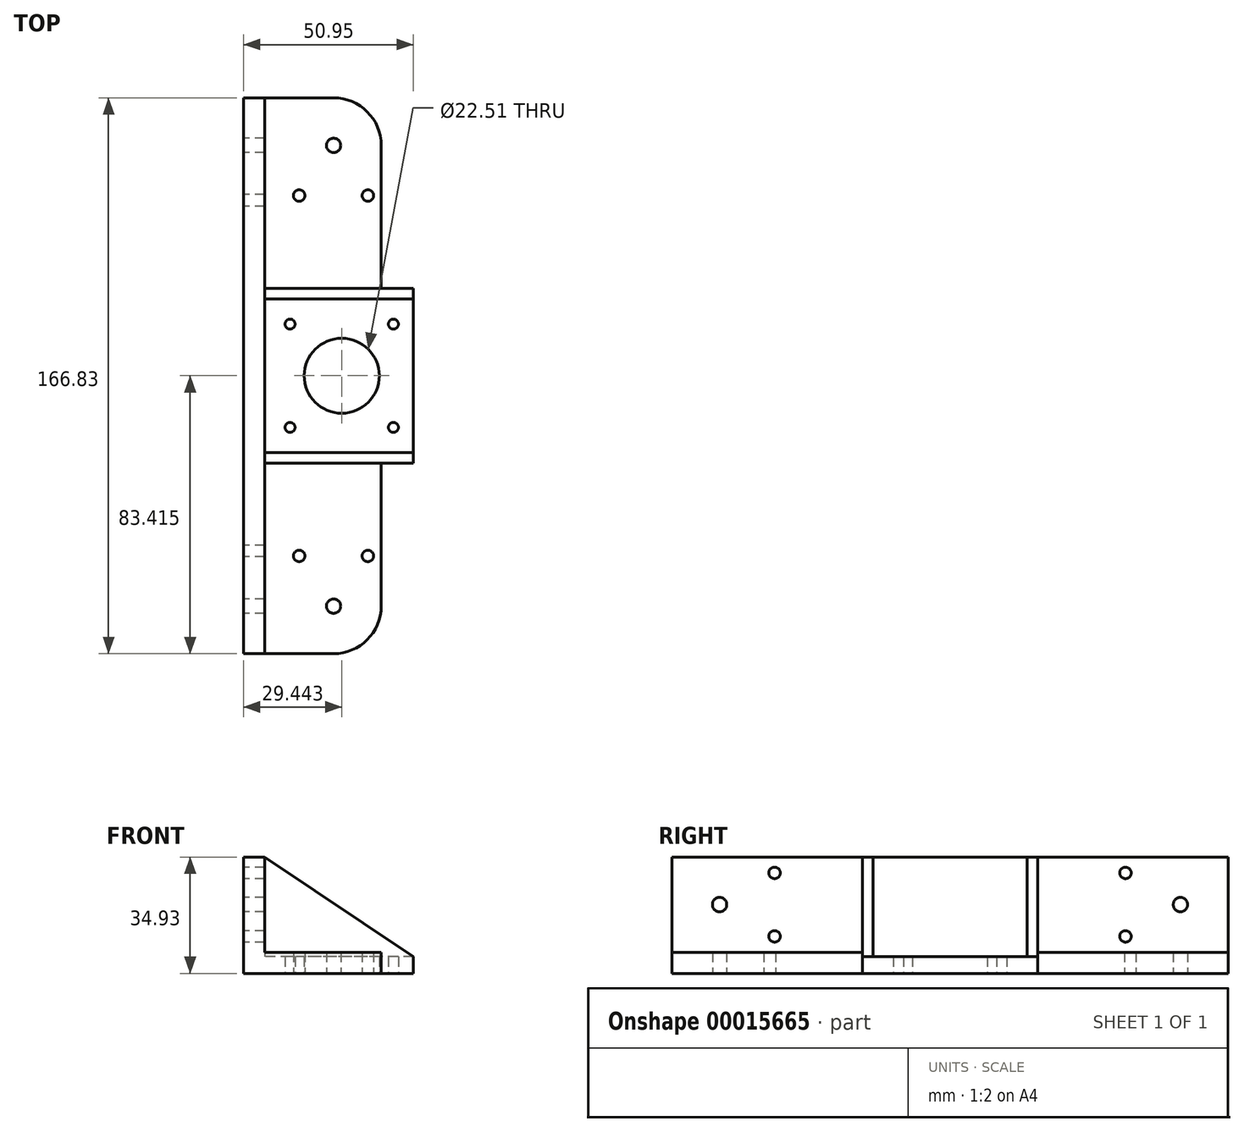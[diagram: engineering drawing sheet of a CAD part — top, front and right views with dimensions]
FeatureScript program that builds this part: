
annotation { "Feature Type Name" : "Feature", "Feature Type Description" : "" }
export const myFeature = defineFeature(function(context is Context, id is Id, definition is map)
    precondition{}
    {
        {
            var Q0;
            Q0=qCreatedBy(makeId("Top.planeOp"),FACE);
            var sketch = newSketch(context, id + "F0", { "sketchPlane" : qUnion([Q0])});
            skLineSegment(sketch, "E0.bottom", {"start": v(0, 0) * mm, "end": v(-26.99, 0) * mm});
            skLineSegment(sketch, "E0.top", {"start": v(0, 166.83) * mm, "end": v(-26.99, 166.83) * mm});
            skLineSegment(sketch, "E0.right", {"start": v(-26.99, 0) * mm, "end": v(-26.99, 166.83) * mm});
            skLineSegment(sketch, "E1.bottom", {"start": v(14.29, 57.15) * mm, "end": v(23.96, 57.15) * mm});
            skLineSegment(sketch, "E1.top", {"start": v(14.29, 109.68) * mm, "end": v(23.96, 109.68) * mm});
            skLineSegment(sketch, "E1.right", {"start": v(23.96, 57.15) * mm, "end": v(23.96, 109.68) * mm});
            skCircle(sketch, "E2", {"center": v(2.45, 83.42) * mm, "radius": 11.25 * mm});
            skLineSegment(sketch, "E3.bottom", {"start": v(17.95, 98.92) * mm, "end": v(-13.05, 98.92) * mm, "construction": true});
            skLineSegment(sketch, "E3.top", {"start": v(17.95, 67.92) * mm, "end": v(-13.05, 67.92) * mm, "construction": true});
            skLineSegment(sketch, "E3.left", {"start": v(17.95, 98.92) * mm, "end": v(17.95, 67.92) * mm, "construction": true});
            skLineSegment(sketch, "E3.right", {"start": v(-13.05, 98.92) * mm, "end": v(-13.05, 67.92) * mm, "construction": true});
            skCircle(sketch, "E4", {"center": v(-13.05, 67.92) * mm, "radius": 1.5 * mm});
            skCircle(sketch, "E5", {"center": v(17.95, 67.92) * mm, "radius": 1.5 * mm});
            skCircle(sketch, "E6", {"center": v(17.95, 98.92) * mm, "radius": 1.5 * mm});
            skCircle(sketch, "E7", {"center": v(-13.05, 98.92) * mm, "radius": 1.5 * mm});
            skLineSegment(sketch, "E8", {"start": v(23.96, 83.42) * mm, "end": v(2.45, 83.42) * mm, "construction": true});
            skLineSegment(sketch, "E9", {"start": v(2.45, 83.42) * mm, "end": v(-26.99, 83.42) * mm, "construction": true});
            skArc(sketch, "E10", {"start": v(0, 0) * mm, "mid": v(10.1, 4.18) * mm, "end": v(14.29, 14.29) * mm});
            skCircle(sketch, "E11", {"center": v(0, 14.29) * mm, "radius": 2.15 * mm});
            skLineSegment(sketch, "E12", {"start": v(14.29, 14.29) * mm, "end": v(14.29, 57.15) * mm});
            skLineSegment(sketch, "E13", {"start": v(14.29, 109.68) * mm, "end": v(14.29, 152.54) * mm});
            skArc(sketch, "E14", {"start": v(14.29, 152.54) * mm, "mid": v(10.1, 162.65) * mm, "end": v(0, 166.83) * mm});
            skCircle(sketch, "E15", {"center": v(0, 152.54) * mm, "radius": 2.15 * mm});
            skLineSegment(sketch, "E16", {"start": v(0, 14.29) * mm, "end": v(0, 29.35) * mm, "construction": true});
            skLineSegment(sketch, "E17", {"start": v(0, 152.54) * mm, "end": v(0, 137.48) * mm, "construction": true});
            skLineSegment(sketch, "E18", {"start": v(-10.32, 137.48) * mm, "end": v(10.32, 137.48) * mm, "construction": true});
            skLineSegment(sketch, "E19", {"start": v(-10.32, 29.35) * mm, "end": v(10.32, 29.35) * mm, "construction": true});
            skCircle(sketch, "E20", {"center": v(-10.32, 29.35) * mm, "radius": 1.73 * mm});
            skCircle(sketch, "E21", {"center": v(10.32, 29.35) * mm, "radius": 1.73 * mm});
            skCircle(sketch, "E22", {"center": v(10.32, 137.48) * mm, "radius": 1.73 * mm});
            skCircle(sketch, "E23", {"center": v(-10.32, 137.48) * mm, "radius": 1.73 * mm});
            skSolve(sketch);
        }
        {
            var Q0;
            Q0 = qSketchRegion(id + "F0", true);
            extrude(context, id + "F1", {"entities" : qUnion([Q0]), "depth" : 5 * mm});
        }
        {
            var Q0;
            Q0=makeQuery(id+"F1.opExtrude","CAP_FACE",FACE,{"disambiguationData":[OSD([sQuery(id+"F0.wireOp",EDGE,"E0.bottom"),sQuery(id+"F0.wireOp",EDGE,"E0.top"),sQuery(id+"F0.wireOp",EDGE,"E0.right"),sQuery(id+"F0.wireOp",EDGE,"sP7DqY9h-m76k-f1Jz-QuWS-NhhGwzX337UM"),sQuery(id+"F0.wireOp",EDGE,"sKsMqQWI-qyKk-qNbw-9HCz-SAMZVSBw6t0P"),sQuery(id+"F0.wireOp",EDGE,"E1.bottom"),sQuery(id+"F0.wireOp",EDGE,"E1.top"),sQuery(id+"F0.wireOp",EDGE,"E1.right")])],"isStart":false});
            var sketch = newSketch(context, id + "F2", { "sketchPlane" : qUnion([Q0])});
            skLineSegment(sketch, "E24.left", {"start": v(-26.99, 0) * mm, "end": v(-26.99, 166.83) * mm});
            skLineSegment(sketch, "E25.top", {"start": v(-20.64, 57.15) * mm, "end": v(23.96, 57.15) * mm});
            skLineSegment(sketch, "E25.left", {"start": v(-20.64, 0) * mm, "end": v(-20.64, 57.15) * mm});
            skLineSegment(sketch, "E26.bottom", {"start": v(23.96, 109.68) * mm, "end": v(-20.64, 109.68) * mm});
            skLineSegment(sketch, "E27", {"start": v(23.96, 57.15) * mm, "end": v(23.96, 60.33) * mm});
            skLineSegment(sketch, "E28", {"start": v(23.96, 109.68) * mm, "end": v(23.96, 106.5) * mm});
            skLineSegment(sketch, "E29.bottom", {"start": v(23.96, 60.33) * mm, "end": v(-20.64, 60.33) * mm});
            skLineSegment(sketch, "E29.top", {"start": v(23.96, 106.5) * mm, "end": v(-20.64, 106.5) * mm});
            skLineSegment(sketch, "E29.left", {"start": v(23.96, 60.33) * mm, "end": v(23.96, 106.5) * mm, "construction": true});
            skLineSegment(sketch, "E29.right", {"start": v(-20.64, 60.33) * mm, "end": v(-20.64, 106.5) * mm});
            skLineSegment(sketch, "E30", {"start": v(-20.64, 109.68) * mm, "end": v(-20.64, 166.83) * mm});
            skLineSegment(sketch, "E31", {"start": v(-20.64, 0) * mm, "end": v(-26.99, 0) * mm});
            skLineSegment(sketch, "E32", {"start": v(-20.64, 166.83) * mm, "end": v(-26.99, 166.83) * mm});
            skSolve(sketch);
        }
        {
            var Q0;
            Q0 = qSketchRegion(id + "F2", true);
            extrude(context, id + "F3", {"entities" : qUnion([Q0]), "operationType" : NewBodyOperationType.ADD, "depth" : 29.93 * mm});
        }
        {
            var Q0;
            Q0=makeQuery(id+"F3.boolean.opBoolean","MERGE",FACE,{"derivedFrom":[makeQuery(id+"F1.opExtrude","SWEPT_FACE",FACE,{"disambiguationData":[OSD([sQuery(id+"F0.wireOp",EDGE,"E1.bottom")])]}),makeQuery(id+"F3.opExtrude","SWEPT_FACE",FACE,{"disambiguationData":[OSD([sQuery(id+"F2.wireOp",EDGE,"E25.top")])]})]});
            var sketch = newSketch(context, id + "F4", { "sketchPlane" : qUnion([Q0])});
            skLineSegment(sketch, "E33.bottom", {"start": v(-20.64, 34.93) * mm, "end": v(23.96, 34.93) * mm});
            skLineSegment(sketch, "E33.top", {"start": v(-20.64, 5) * mm, "end": v(23.96, 5) * mm, "construction": true});
            skLineSegment(sketch, "E33.left", {"start": v(-20.64, 34.93) * mm, "end": v(-20.64, 5) * mm, "construction": true});
            skLineSegment(sketch, "E33.right", {"start": v(23.96, 34.93) * mm, "end": v(23.96, 5) * mm});
            skLineSegment(sketch, "E34", {"start": v(-20.64, 34.93) * mm, "end": v(23.96, 5) * mm});
            skSolve(sketch);
        }
        {
            var Q0;
            Q0 = qSketchRegion(id + "F4", true);
            var Q1;
            Q1=makeQuery(id+"F3.boolean.opBoolean","MERGE",FACE,{"derivedFrom":[makeQuery(id+"F1.opExtrude","SWEPT_FACE",FACE,{"disambiguationData":[OSD([sQuery(id+"F0.wireOp",EDGE,"E1.top")])]}),makeQuery(id+"F3.opExtrude","SWEPT_FACE",FACE,{"disambiguationData":[OSD([sQuery(id+"F2.wireOp",EDGE,"E26.bottom")])]})]});
            extrude(context, id + "F5", {"entities" : qUnion([Q0]), "operationType" : NewBodyOperationType.REMOVE, "endBound" : BoundingType.UP_TO_SURFACE, "oppositeDirection" : true, "endBoundEntityFace" : qUnion([Q1]), "depth" : 25.4 * mm});
        }
        {
            var Q0;
            Q0=makeQuery(id+"F3.boolean.opBoolean","MERGE",FACE,{"derivedFrom":[makeQuery(id+"F1.opExtrude","SWEPT_FACE",FACE,{"disambiguationData":[OSD([sQuery(id+"F0.wireOp",EDGE,"E0.right")])]}),makeQuery(id+"F3.opExtrude","SWEPT_FACE",FACE,{"disambiguationData":[OSD([sQuery(id+"F2.wireOp",EDGE,"E24.left")])]})]});
            var sketch = newSketch(context, id + "F6", { "sketchPlane" : qUnion([Q0])});
            skLineSegment(sketch, "E35", {"start": v(-166.83, 20.64) * mm, "end": v(-152.54, 20.64) * mm, "construction": true});
            skLineSegment(sketch, "E36", {"start": v(0, 20.64) * mm, "end": v(-14.29, 20.64) * mm, "construction": true});
            skCircle(sketch, "E37", {"center": v(-152.54, 20.64) * mm, "radius": 2.15 * mm});
            skCircle(sketch, "E38", {"center": v(-14.29, 20.64) * mm, "radius": 2.15 * mm});
            skLineSegment(sketch, "E39", {"start": v(-83.42, 20.64) * mm, "end": v(-83.42, 34.93) * mm, "construction": true});
            skLineSegment(sketch, "E40.bottom", {"start": v(-136.05, 30.16) * mm, "end": v(-30.79, 30.16) * mm, "construction": true});
            skLineSegment(sketch, "E40.top", {"start": v(-136.05, 11.11) * mm, "end": v(-30.79, 11.11) * mm, "construction": true});
            skLineSegment(sketch, "E40.left", {"start": v(-136.05, 30.16) * mm, "end": v(-136.05, 11.11) * mm, "construction": true});
            skLineSegment(sketch, "E40.right", {"start": v(-30.79, 30.16) * mm, "end": v(-30.79, 11.11) * mm, "construction": true});
            skPoint(sketch, "E40.middle", {"position": v(-83.42, 20.64) * mm});
            skLineSegment(sketch, "E41", {"start": v(-152.54, 20.64) * mm, "end": v(-136.05, 20.64) * mm, "construction": true});
            skCircle(sketch, "E42", {"center": v(-136.05, 30.16) * mm, "radius": 1.73 * mm});
            skCircle(sketch, "E43", {"center": v(-136.05, 11.11) * mm, "radius": 1.73 * mm});
            skCircle(sketch, "E44", {"center": v(-30.79, 11.11) * mm, "radius": 1.73 * mm});
            skCircle(sketch, "E45", {"center": v(-30.79, 30.16) * mm, "radius": 1.73 * mm});
            skLineSegment(sketch, "E46", {"start": v(-83.42, 11.11) * mm, "end": v(-83.42, 5) * mm, "construction": true});
            skSolve(sketch);
        }
        {
            var Q0;
            Q0 = qSketchRegion(id + "F6", true);
            var Q1;
            Q1=makeQuery(id+"F3.opExtrude","SWEPT_FACE",FACE,{"disambiguationData":[OSD([sQuery(id+"F2.wireOp",EDGE,"E29.right")])]});
            extrude(context, id + "F7", {"entities" : qUnion([Q0]), "operationType" : NewBodyOperationType.REMOVE, "endBound" : BoundingType.UP_TO_SURFACE, "oppositeDirection" : true, "endBoundEntityFace" : qUnion([Q1]), "depth" : 25.4 * mm});
        }
        {
            var Q0;
            {var subQ0=sQuery(id+"F0.wireOp",EDGE,"E10");var subQ1=sQuery(id+"F0.wireOp",EDGE,"E1.bottom");var subQ2=sQuery(id+"F0.wireOp",EDGE,"E11");var subQ3=sQuery(id+"F0.wireOp",EDGE,"E0.bottom");var subQ4=sQuery(id+"F0.wireOp",EDGE,"E12");Q0=makeQuery(id+"F3.boolean.opBoolean","SPLIT",FACE,{"disambiguationData":[TD([makeQuery(id+"F1.opExtrude","SWEPT_FACE",FACE,{"disambiguationData":[OSD([subQ3])]})])],"derivedFrom":makeQuery(id+"F1.opExtrude","CAP_FACE",FACE,{"disambiguationData":[OSD([subQ3,sQuery(id+"F0.wireOp",EDGE,"E0.top"),sQuery(id+"F0.wireOp",EDGE,"E0.right"),subQ1,sQuery(id+"F0.wireOp",EDGE,"E1.top"),sQuery(id+"F0.wireOp",EDGE,"E1.right"),sQuery(id+"F0.wireOp",EDGE,"E2"),sQuery(id+"F0.wireOp",EDGE,"E4"),sQuery(id+"F0.wireOp",EDGE,"E5"),sQuery(id+"F0.wireOp",EDGE,"E6"),sQuery(id+"F0.wireOp",EDGE,"E7"),subQ0,subQ2,subQ4,sQuery(id+"F0.wireOp",EDGE,"E13"),sQuery(id+"F0.wireOp",EDGE,"E14"),sQuery(id+"F0.wireOp",EDGE,"E15")])],"isStart":false})});}
            var Q1;
            {var subQ0=sQuery(id+"F0.wireOp",EDGE,"E13");var subQ1=sQuery(id+"F0.wireOp",EDGE,"E1.top");var subQ2=sQuery(id+"F0.wireOp",EDGE,"E15");var subQ3=sQuery(id+"F0.wireOp",EDGE,"E14");var subQ4=sQuery(id+"F0.wireOp",EDGE,"E0.top");Q1=makeQuery(id+"F3.boolean.opBoolean","SPLIT",FACE,{"disambiguationData":[TD([makeQuery(id+"F1.opExtrude","SWEPT_FACE",FACE,{"disambiguationData":[OSD([subQ4])]})])],"derivedFrom":makeQuery(id+"F1.opExtrude","CAP_FACE",FACE,{"disambiguationData":[OSD([sQuery(id+"F0.wireOp",EDGE,"E0.bottom"),subQ4,sQuery(id+"F0.wireOp",EDGE,"E0.right"),sQuery(id+"F0.wireOp",EDGE,"E1.bottom"),subQ1,sQuery(id+"F0.wireOp",EDGE,"E1.right"),sQuery(id+"F0.wireOp",EDGE,"E2"),sQuery(id+"F0.wireOp",EDGE,"E4"),sQuery(id+"F0.wireOp",EDGE,"E5"),sQuery(id+"F0.wireOp",EDGE,"E6"),sQuery(id+"F0.wireOp",EDGE,"E7"),sQuery(id+"F0.wireOp",EDGE,"E10"),sQuery(id+"F0.wireOp",EDGE,"E11"),sQuery(id+"F0.wireOp",EDGE,"E12"),subQ0,subQ3,subQ2])],"isStart":false})});}
            extrude(context, id + "F8", {"entities" : qUnion([Q0, Q1]), "operationType" : NewBodyOperationType.ADD, "depth" : 1.35 * mm});
        }
    });
